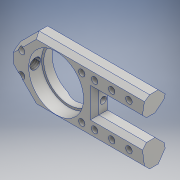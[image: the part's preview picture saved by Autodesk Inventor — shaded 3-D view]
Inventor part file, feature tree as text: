
AUTODESK INVENTOR PART (.ipt)
format: ipt  version: 2017 SP1 (Build 210196100, 196)  size: 261,632 bytes
history: native  units: mm
features: sketch x11, extrude x6, hole x5, chamfer x5
ambient origin geometry x8: Origin, YZ Plane, XZ Plane, XY Plane, X Axis, Y Axis, Z Axis, Center Point
bodies: Solid1 (feature_tree)
feature tree (27):
  extrude  "Extrusion1"  Depth=15.0mm
  extrude  "Extrusion2"  Depth=70.0mm
  extrude  "Extrusion3"  Depth=12.8mm
  extrude  "Extrusion4"  Depth=55.0mm
  hole  "Hole1"  [1 undecoded]
  extrude  "Extrusion5"  Depth=2.5mm
  chamfer  "Chamfer1"  Distance=6.0mm
  chamfer  "Chamfer2"  Distance=5.0mm Angle=45.0deg
  hole  "Hole2"  [1 undecoded]
  hole  "Hole3"  [1 undecoded]
  chamfer  "Chamfer3"  Distance=1.0mm
  chamfer  "Chamfer4"  Distance=1.0mm Angle=45.0deg
  extrude  "Extrusion6"  [1 undecoded]
  chamfer  "Chamfer5"  [1 undecoded]
  hole  "Hole4"  [1 undecoded]
  hole  "Hole5"  [1 undecoded]
  sketch  "Sketch1"  dims[d0=65.0mm d1=15.0mm]
  sketch  "Sketch2"  dims[d2=6.0mm d3=0.0mm d4=70.0mm]
  sketch  "Sketch3"  dims[d5=6.0mm d6=0.0mm d7=12.8mm]
  sketch  "Sketch4"  dims[d8=4.0mm d9=0.0mm d10=55.0mm]
  sketch  "Sketch5"  dims[d11=11.8mm d12=4.0mm d13=0.0mm]
  sketch  "Sketch6"  dims[d14=2.459mm d15=6.0mm d16=4.0mm d17=2.0mm d18=90.0deg d19=8.8mm d20=20.594885mm d21=2.5mm]
  sketch  "Sketch7"  dims[d22=12.0mm]
  sketch  "Sketch8"  dims[d23=5.0mm d24=6.0mm d25=0.0mm d26=5.0mm d27=2.0mm d28=45.0deg]
  sketch  "Sketch9"  dims[d29=2.0mm d30=2.0mm d31=45.0deg]
  sketch  "Sketch10"  dims[d32=1.5mm d33=6.0mm d34=4.0mm d35=2.0mm d36=90.0deg d37=8.0mm d38=20.594885mm]
  sketch  "Sketch11"  dims[d39=1.5mm d40=6.0mm d41=4.0mm d42=2.0mm d43=90.0deg d44=8.0mm d45=20.594885mm d46=1.0mm d47=2.0mm d48=45.0deg d49=1.0mm d50=2.0mm d51=45.0deg d52=1.0mm d53=0.0mm d54=1.0mm d55=2.0mm d56=45.0deg d57=1.5mm d58=6.0mm d59=4.0mm d60=2.0mm d61=90.0deg d62=8.0mm d63=20.594885mm d64=1.5mm d65=6.0mm d66=4.0mm d67=2.0mm d68=90.0deg d69=8.0mm d70=20.594885mm]
note: 7 required parameter values undecoded (feature->parameter linkage not recoverable at this tier; creation-order binding heuristic only, values carry confidence <= 0.55)
